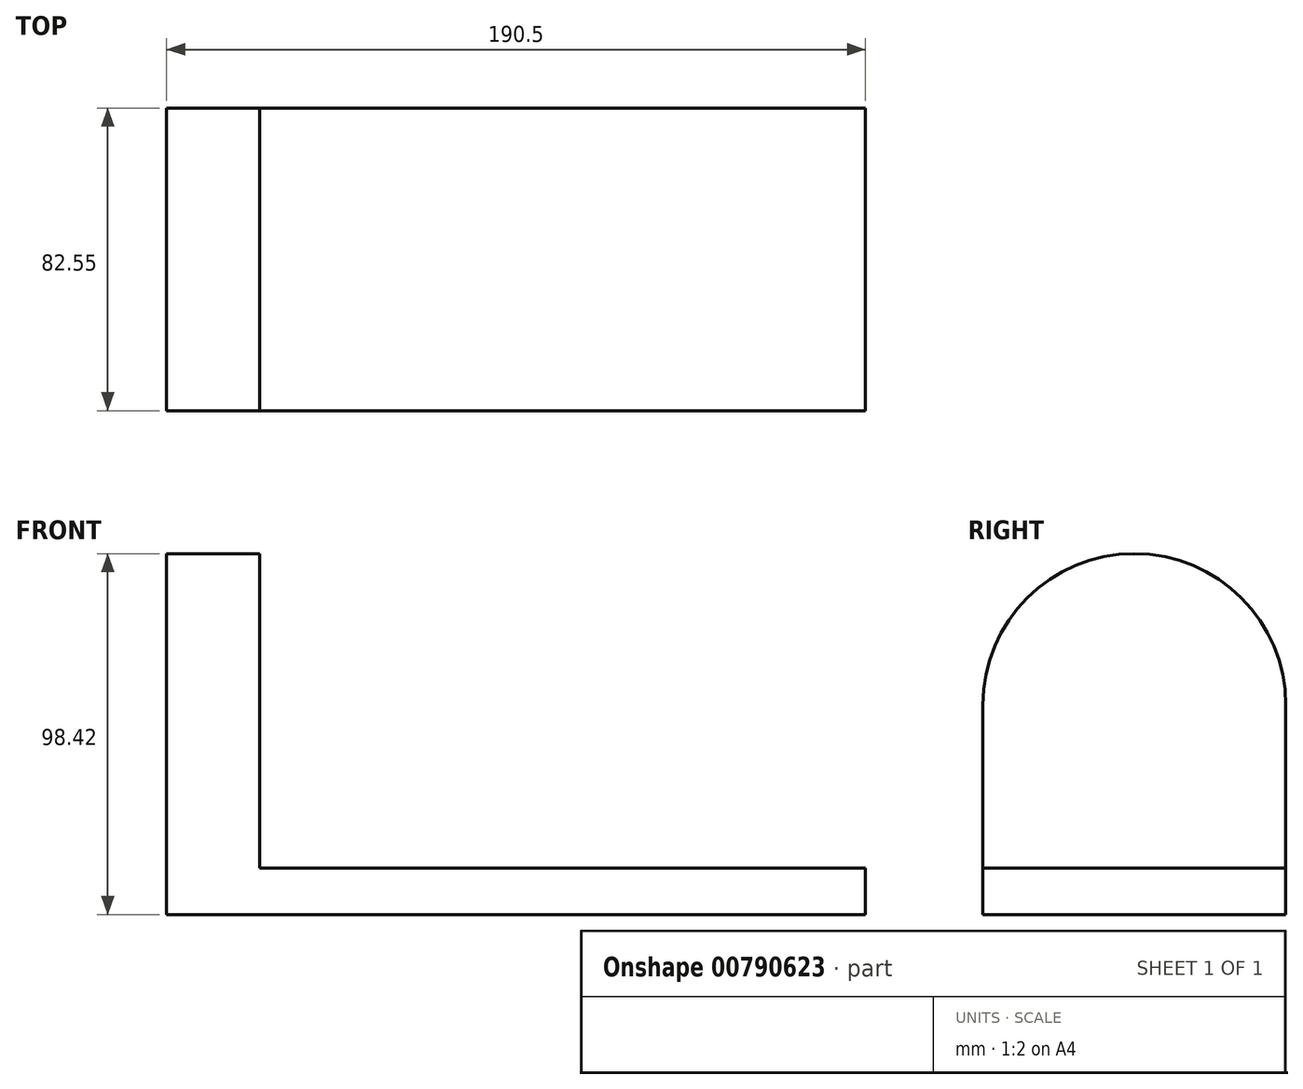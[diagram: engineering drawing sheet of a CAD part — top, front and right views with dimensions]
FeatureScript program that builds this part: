
annotation { "Feature Type Name" : "Feature", "Feature Type Description" : "" }
export const myFeature = defineFeature(function(context is Context, id is Id, definition is map)
    precondition{}
    {
        {
            var Q0;
            Q0=qCreatedBy(makeId("Front.planeOp"),FACE);
            var sketch = newSketch(context, id + "F0", { "sketchPlane" : qUnion([Q0])});
            skLineSegment(sketch, "E0", {"start": v(0, 0) * mm, "end": v(190.5, 0) * mm});
            skLineSegment(sketch, "E1", {"start": v(190.5, 0) * mm, "end": v(190.5, 12.7) * mm});
            skLineSegment(sketch, "E2", {"start": v(190.5, 12.7) * mm, "end": v(25.4, 12.7) * mm});
            skLineSegment(sketch, "E3", {"start": v(25.4, 12.7) * mm, "end": v(25.4, 156.76) * mm});
            skLineSegment(sketch, "E4", {"start": v(25.4, 156.76) * mm, "end": v(0, 156.76) * mm});
            skLineSegment(sketch, "E5", {"start": v(0, 156.76) * mm, "end": v(0, 0) * mm});
            skSolve(sketch);
        }
        {
            var Q0;
            Q0 = qSketchRegion(id + "F0", true);
            extrude(context, id + "F1", {"entities" : qUnion([Q0]), "depth" : 82.55 * mm, "offsetDistance" : 25.4 * mm});
        }
        {
            var Q0;
            Q0=makeQuery(id+"F1.opExtrude","SWEPT_FACE",FACE,{"disambiguationData":[OSD([sQuery(id+"F0.wireOp",EDGE,"E5")])]});
            var sketch = newSketch(context, id + "F2", { "sketchPlane" : qUnion([Q0])});
            skLineSegment(sketch, "E6", {"start": v(0, 0) * mm, "end": v(0, 57.15) * mm, "construction": true});
            skLineSegment(sketch, "E7", {"start": v(0, 57.15) * mm, "end": v(82.55, 57.15) * mm, "construction": true});
            skLineSegment(sketch, "E8", {"start": v(82.55, 57.15) * mm, "end": v(82.55, 0) * mm, "construction": true});
            skLineSegment(sketch, "E9", {"start": v(41.28, 57.15) * mm, "end": v(41.28, 15.88) * mm, "construction": true});
            skLineSegment(sketch, "E10", {"start": v(41.28, 57.15) * mm, "end": v(41.28, 98.43) * mm, "construction": true});
            skArc(sketch, "E11", {"start": v(82.55, 57.15) * mm, "mid": v(41.28, 98.43) * mm, "end": v(0, 57.15) * mm});
            skSolve(sketch);
        }
        {
            var Q0;
            {var subQ0=sQuery(id+"F2.wireOp",EDGE,"E11");Q0=makeQuery(id+"F2.imprint","IMPRINT",FACE,{"disambiguationData":[TD([[makeQuery(id+"F2.imprint","IMPRINT",EDGE,{"derivedFrom":subQ0}),-1.0]])]});}
            extrude(context, id + "F3", {"entities" : qUnion([Q0]), "operationType" : NewBodyOperationType.REMOVE, "endBound" : BoundingType.THROUGH_ALL, "oppositeDirection" : true, "depth" : 25.4 * mm, "offsetDistance" : 25.4 * mm});
        }
    });
